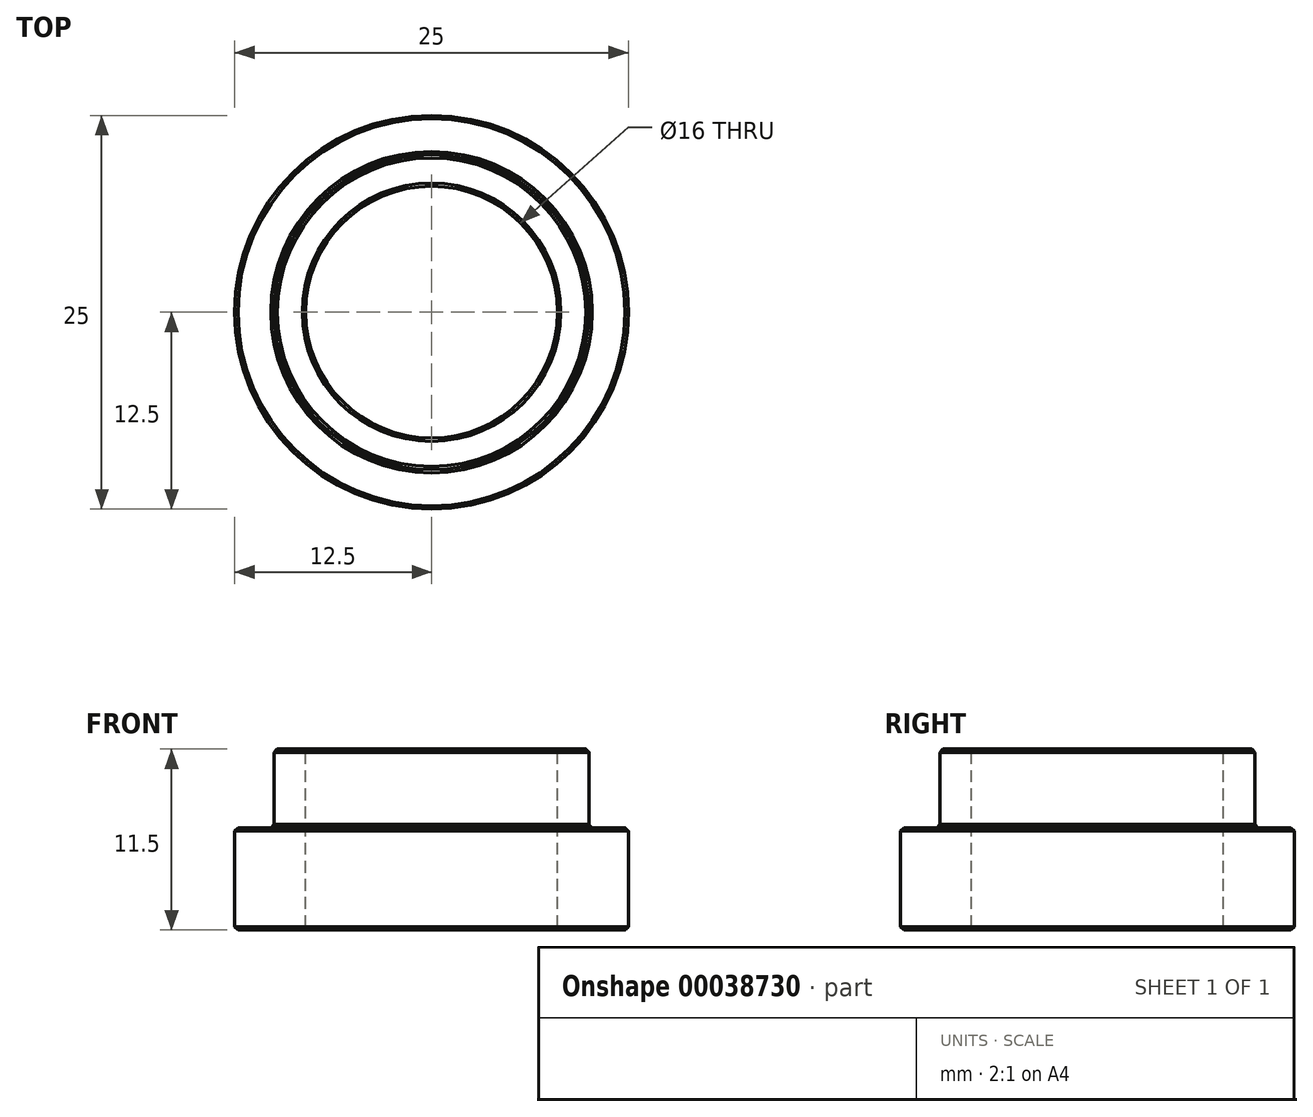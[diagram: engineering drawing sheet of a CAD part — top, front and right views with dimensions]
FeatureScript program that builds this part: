
annotation { "Feature Type Name" : "Feature", "Feature Type Description" : "" }
export const myFeature = defineFeature(function(context is Context, id is Id, definition is map)
    precondition{}
    {
        {
            var Q0;
            Q0=qCreatedBy(makeId("Top.planeOp"),FACE);
            var sketch = newSketch(context, id + "F0", { "sketchPlane" : qUnion([Q0])});
            skCircle(sketch, "E0", {"center": v(0, 0) * mm, "radius": 12.5 * mm});
            skSolve(sketch);
        }
        {
            var Q0;
            Q0=qSketchRegion(id+"F0",true);
            extrude(context, id + "F1", {"entities" : qUnion([Q0]), "depth" : 6.5 * mm});
        }
        {
            var Q0;
            Q0=makeQuery(id+"F1.opExtrude","CAP_FACE",FACE,{"disambiguationData":[OSD([sQuery(id+"F0.wireOp",EDGE,"E0")])],"isStart":false});
            var sketch = newSketch(context, id + "F2", { "sketchPlane" : qUnion([Q0])});
            skCircle(sketch, "E1", {"center": v(0, 0) * mm, "radius": 10 * mm});
            skSolve(sketch);
        }
        {
            var Q0;
            Q0=qSketchRegion(id+"F2",true);
            extrude(context, id + "F3", {"entities" : qUnion([Q0]), "operationType" : NewBodyOperationType.ADD, "depth" : 5 * mm});
        }
        {
            var Q0;
            Q0=makeQuery(id+"F3.opExtrude","CAP_FACE",FACE,{"disambiguationData":[OSD([sQuery(id+"F2.wireOp",EDGE,"E1")])],"isStart":false});
            var sketch = newSketch(context, id + "F4", { "sketchPlane" : qUnion([Q0])});
            skCircle(sketch, "E2", {"center": v(0, 0) * mm, "radius": 8 * mm});
            skSolve(sketch);
        }
        {
            var Q0;
            Q0=qSketchRegion(id+"F4",true);
            extrude(context, id + "F5", {"entities" : qUnion([Q0]), "operationType" : NewBodyOperationType.REMOVE, "endBound" : BoundingType.THROUGH_ALL, "oppositeDirection" : true, "depth" : 25 * mm});
        }
        {
            var Q0;
            Q0=makeQuery(id+"F3.opExtrude","CAP_FACE",FACE,{"disambiguationData":[OSD([sQuery(id+"F2.wireOp",EDGE,"E1")])],"isStart":false});
            var Q1;
            Q1=makeQuery(id+"F1.opExtrude","CAP_FACE",FACE,{"disambiguationData":[OSD([sQuery(id+"F0.wireOp",EDGE,"E0")])],"isStart":false});
            var Q2;
            Q2=makeQuery(id+"F1.opExtrude","CAP_FACE",FACE,{"disambiguationData":[OSD([sQuery(id+"F0.wireOp",EDGE,"E0")])],"isStart":true});
            chamfer(context, id + "F6", {"entities" : qUnion([Q0, Q1, Q2]), "width" : 0.2 * mm, "tangentPropagation" : true});
        }
    });
